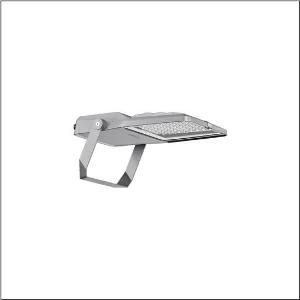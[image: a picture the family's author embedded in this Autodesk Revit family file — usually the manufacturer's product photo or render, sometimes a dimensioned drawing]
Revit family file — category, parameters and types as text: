
# Revit family: floodlight_fl_21_iq_mini___pl52_5xa7772d5d1a_a443
name_source: partatom
category: Lighting Fixtures
units: mm (PartAtom-declared; Revit-internal decimal feet)

## family parameters
Cut with Voids When Loaded = No
Host = Face
Light Source = No
Part Type = Normal
Room Calculation Point = No
Round Connector Dimension = Use Diameter
Shared = No

## types (1)
- --- (1 x LED, 16640 lm, 143 W, 4000K)
    Apparent Load = 143 VA
    CIE Flux Codes = 26 60 98 100 100
    Color Rendering = 80
    Color Temperature = 4000K
    Default Elevation = 1800 mm
    Description = Floodlight FL 21 iQ mini, floodlight, primary light control with lens, of PMMA, primary optical cover: protective disc, of toughened safety glass, transparent, light distribution: PL52, light emission: direct distribution, installation type: surface-mounted, lamps: LED, High Power LED, rated values: 16.640lm | 143W | 116,4lm/W (begin service life); end service life: 16.640lm | 151,6W; at 50% lumin. flux: 8.320lm | 60,6W | 137,3lm/W, colour temperature: 4000K, colour rendering: CRI > 80, light colour: 840, light setting 1 begin service life: 100% | 16.640lm | 143W | 116,4lm/W | 4.000K, light setting 1 end service life: 151,6W, further light settings possible, control: Street-Remote, Auto-Match, Temp-Guard, Night-Set, Smart-Wire, Desk-Remote (wireless, voltage-free reading and setting of iQ features in the workshop via application-optimized NFC function/RFID function), optimised constant luminous flux control (CLO 2.0), pre-setting: linear dimming characteristic, with terminal, 6-pole, mains connection: 220..240V, AC, 50/60Hz, luminaire housing, of diecast aluminium, powder-coated, SITECO metallic grey (DB 702S), corrosivity category C5 mid according to DIN EN ISO 12944suitable for swimming poolschlorine-resistant, sealing non-destructively replaceable, mounting bracket, of steel, galvanised, powder-coated, SITECO metallic grey (DB 702S), protection rating (complete): IP66, insulation class (complete): insulation class II (safety insulation), certification: CE, ENEC, VDE, protection symbol: D, impact resistance: IK08, permissible operating ambient temperature: -40..+40°C, permissible operating ambient temperature for outdoor applications: -40..+50°C, standard: DIN EN 12944, LABS conformity tested according to VDMA 24364:2018-05, packaging unit: 1 piece

Light Distribution: PL52
    Height = 70 mm
    Lamp = 1 x LED
    Lamp Light Flux = 16640 lm
    Lamp Power = 143 W
    Lamp count = 1
    Length = 485 mm
    Luminous efficacy = 116 lm/W
    Manufacturer = Siteco
    ModVariant = No
    Model = 5XA7772D5D1A
    Mounting Place = Pole
    Mounting Type = Pole annexe
    Number of Poles = 1
    OnlyDefault = Yes
    Power Factor = 1
    Product Name = Floodlight FL 21 iQ mini | PL52
    Product group = floodlight | pylon annexe
    ProductGroupID = 6201
    Protection Class = Protection class II
    Protection Degree = IP 66
    RLX_Detail_Level = 1
    RLX_Emergency_Light_Flux = 0 lm
    RLX_Emergency_Type = 0
    RLX_Emergency_Type_DB = No
    RlxData = <blob elided: 96953 chars, md5=1d1ae6c4>
    Socket = socket
    Standby Power = 0 W
    System Light Flux = 16640 lm
    System Power = 143 W
    Type Comments = factory setting: luminous flux: 100 % | dim-lin: 254 | 730 mA
    Type Image = l_1006845.jpg
    URL = http://relux.com
    VarID = @adj_164547
    Voltage = 0 V
    Weight = 0.00 kg
    Width = 337 mm

## geometry (parser evidence)
native form markers: Blend x4, Sweep x13
no freeform markers — native parametric forms only
